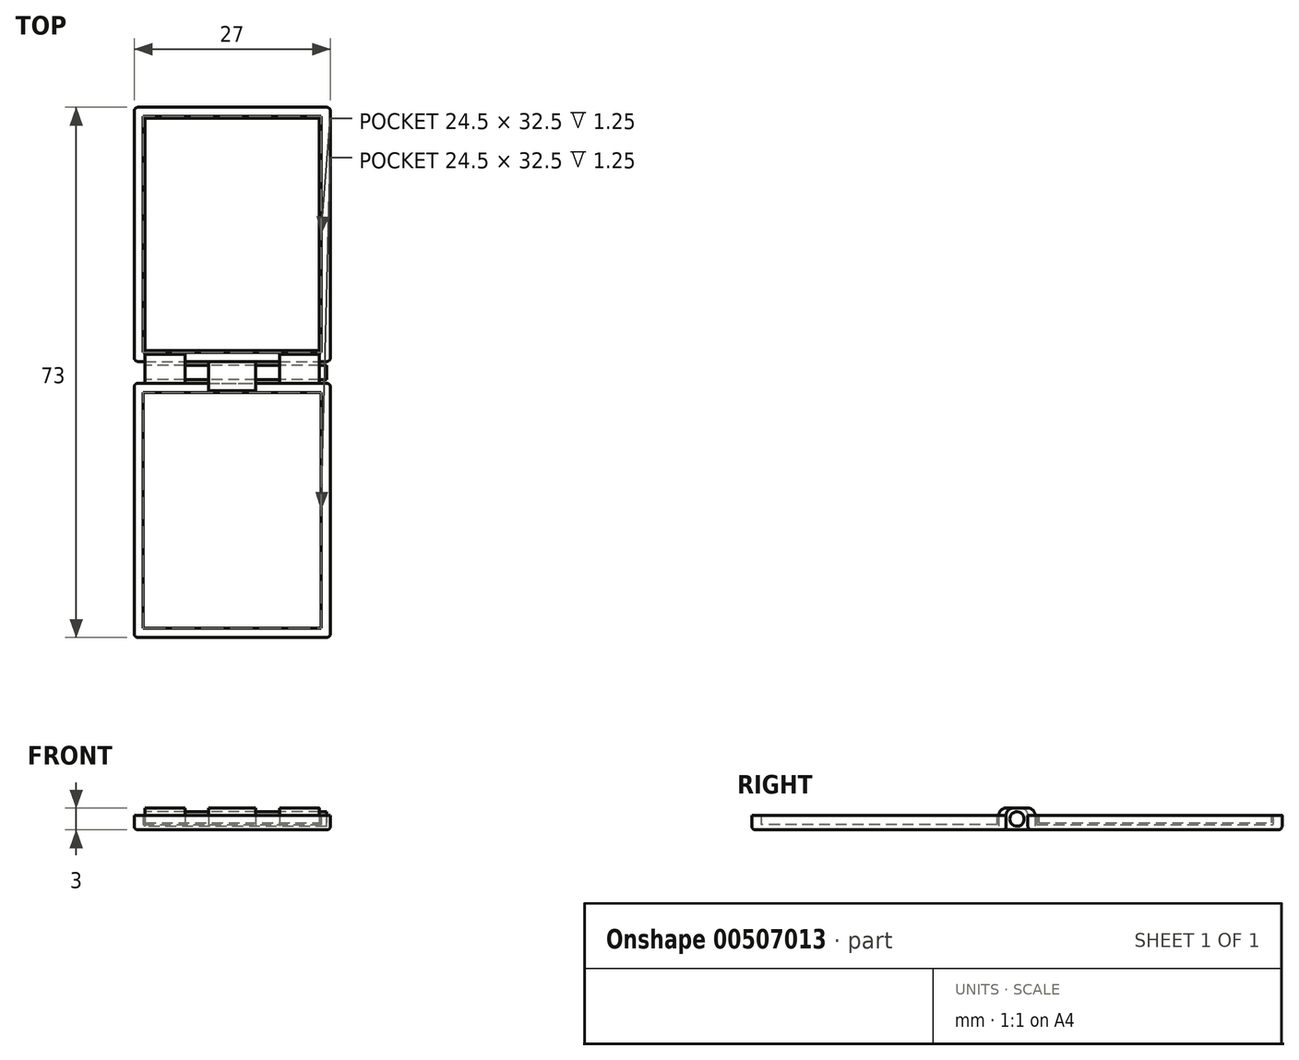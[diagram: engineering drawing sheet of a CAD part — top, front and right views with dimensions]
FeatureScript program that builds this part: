
annotation { "Feature Type Name" : "Feature", "Feature Type Description" : "" }
export const myFeature = defineFeature(function(context is Context, id is Id, definition is map)
    precondition{}
    {
        {
            var Q0;
            Q0=qCreatedBy(makeId("Top.planeOp"),FACE);
            var sketch = newSketch(context, id + "F0", { "sketchPlane" : qUnion([Q0])});
            skLineSegment(sketch, "E0.bottom", {"start": v(0, 0) * mm, "end": v(24, 0) * mm});
            skLineSegment(sketch, "E0.top", {"start": v(0, 32) * mm, "end": v(24, 32) * mm});
            skLineSegment(sketch, "E0.left", {"start": v(0, 0) * mm, "end": v(0, 32) * mm});
            skLineSegment(sketch, "E0.right", {"start": v(24, 0) * mm, "end": v(24, 32) * mm});
            skSolve(sketch);
        }
        {
            var Q0;
            Q0=makeQuery(id+"F0.imprint","IMPRINT",FACE,{"disambiguationData":[TD([[makeQuery(id+"F0.imprint","IMPRINT",EDGE,{"derivedFrom":sQuery(id+"F0.wireOp",EDGE,"E0.bottom")}),1.0]])]});
            extrude(context, id + "F1", {"entities" : qUnion([Q0]), "depth" : 2.1 * mm});
        }
        {
            var Q0;
            Q0=qCreatedBy(makeId("Top.planeOp"),FACE);
            cPlane(context, id + "F2", {"entities" : qUnion([Q0]), "cplaneType" : CPlaneType.OFFSET, "offset" : 1 * mm, "oppositeDirection" : true, "width" : 150 * mm, "height" : 150 * mm});
        }
        {
            var Q0;
            Q0=qCreatedBy(id+"F2.planeOp",FACE);
            var sketch = newSketch(context, id + "F3", { "sketchPlane" : qUnion([Q0])});
            skLineSegment(sketch, "E1.0.0", {"start": v(24, 32) * mm, "end": v(0, 32) * mm});
            skLineSegment(sketch, "E1.0.1", {"start": v(0, 32) * mm, "end": v(0, 0) * mm});
            skLineSegment(sketch, "E1.0.2", {"start": v(0, 0) * mm, "end": v(24, 0) * mm});
            skLineSegment(sketch, "E1.0.3", {"start": v(24, 0) * mm, "end": v(24, 32) * mm});
            skLineSegment(sketch, "E2.0", {"start": v(25.5, 33.5) * mm, "end": v(-1.5, 33.5) * mm});
            skLineSegment(sketch, "E2.1", {"start": v(25.5, -1.5) * mm, "end": v(25.5, 33.5) * mm});
            skLineSegment(sketch, "E2.2", {"start": v(-1.5, -1.5) * mm, "end": v(25.5, -1.5) * mm});
            skLineSegment(sketch, "E2.3", {"start": v(-1.5, 33.5) * mm, "end": v(-1.5, -1.5) * mm});
            skSolve(sketch);
        }
        {
            var Q0;
            Q0=makeQuery(id+"F3.imprint","IMPRINT",FACE,{"disambiguationData":[TD([[makeQuery(id+"F3.imprint","IMPRINT",EDGE,{"derivedFrom":sQuery(id+"F3.wireOp",EDGE,"E1.0.0")}),1.0]])]});
            var Q1;
            Q1=makeQuery(id+"F3.imprint","IMPRINT",FACE,{"disambiguationData":[TD([[makeQuery(id+"F3.imprint","IMPRINT",EDGE,{"derivedFrom":sQuery(id+"F3.wireOp",EDGE,"E1.0.0")}),-1.0]])]});
            extrude(context, id + "F4", {"entities" : qUnion([Q0, Q1]), "depth" : 4 * mm});
        }
        {
            var Q0;
            Q0=makeQuery(id+"F4.opExtrude","SWEPT_FACE",FACE,{"disambiguationData":[OSD([sQuery(id+"F3.wireOp",EDGE,"E2.1")])]});
            var sketch = newSketch(context, id + "F5", { "sketchPlane" : qUnion([Q0])});
            skPoint(sketch, "E3", {"position": v(-1.5, 1) * mm});
            skPoint(sketch, "E4", {"position": v(33.5, 1) * mm});
            skLineSegment(sketch, "E5.bottom", {"start": v(-1.5, 1) * mm, "end": v(33.5, 1) * mm});
            skLineSegment(sketch, "E5.top", {"start": v(-1.5, 3) * mm, "end": v(33.5, 3) * mm});
            skLineSegment(sketch, "E5.left", {"start": v(-1.5, 1) * mm, "end": v(-1.5, 3) * mm});
            skLineSegment(sketch, "E5.right", {"start": v(33.5, 1) * mm, "end": v(33.5, 3) * mm});
            skSolve(sketch);
        }
        {
            var Q0;
            Q0=makeQuery(id+"F1.opExtrude","SWEPT_BODY",BODY,{"disambiguationData":[OSD([sQuery(id+"F0.wireOp",EDGE,"E0.bottom"),sQuery(id+"F0.wireOp",EDGE,"E0.top"),sQuery(id+"F0.wireOp",EDGE,"E0.left"),sQuery(id+"F0.wireOp",EDGE,"E0.right")])]});
            var Q1;
            Q1=makeQuery(id+"F4.opExtrude","SWEPT_BODY",BODY,{"disambiguationData":[OSD([sQuery(id+"F3.wireOp",EDGE,"E2.0"),sQuery(id+"F3.wireOp",EDGE,"E2.1"),sQuery(id+"F3.wireOp",EDGE,"E2.2"),sQuery(id+"F3.wireOp",EDGE,"E2.3")])]});
            var Q2;
            Q2=makeQuery(id+"F1.opExtrude","SWEPT_FACE",FACE,{"disambiguationData":[OSD([sQuery(id+"F0.wireOp",EDGE,"E0.right")])]});
            var Q3;
            Q3=makeQuery(id+"F1.opExtrude","SWEPT_FACE",FACE,{"disambiguationData":[OSD([sQuery(id+"F0.wireOp",EDGE,"E0.left")])]});
            booleanBodies(context, id + "F6", {"operationType" : BooleanOperationType.SUBTRACTION, "tools" : qUnion([Q0]), "targets" : qUnion([Q1]), "offset" : true, "offsetAll" : true, "entitiesToOffset" : qUnion([Q2, Q3]), "offsetDistance" : 0.25 * mm, "keepTools" : true});
        }
        {
            var Q0;
            Q0=makeQuery(id+"F4.opExtrude","SWEPT_EDGE",EDGE,{"disambiguationData":[OSD([sQuery(id+"F3.wireOp",EDGE,"E2.2"),sQuery(id+"F3.wireOp",EDGE,"E2.3")])]});
            var Q1;
            Q1=makeQuery(id+"F4.opExtrude","SWEPT_EDGE",EDGE,{"disambiguationData":[OSD([sQuery(id+"F3.wireOp",EDGE,"E2.1"),sQuery(id+"F3.wireOp",EDGE,"E2.2")])]});
            var Q2;
            Q2=makeQuery(id+"F4.opExtrude","SWEPT_EDGE",EDGE,{"disambiguationData":[OSD([sQuery(id+"F3.wireOp",EDGE,"E2.0"),sQuery(id+"F3.wireOp",EDGE,"E2.1")])]});
            var Q3;
            Q3=makeQuery(id+"F4.opExtrude","SWEPT_EDGE",EDGE,{"disambiguationData":[OSD([sQuery(id+"F3.wireOp",EDGE,"E2.0"),sQuery(id+"F3.wireOp",EDGE,"E2.3")])]});
            var Q4;
            Q4=makeQuery(id+"F4.opExtrude","CAP_EDGE",EDGE,{"disambiguationData":[OSD([sQuery(id+"F3.wireOp",EDGE,"E2.3")])],"isStart":false});
            var Q5;
            Q5=makeQuery(id+"F4.opExtrude","CAP_EDGE",EDGE,{"disambiguationData":[OSD([sQuery(id+"F3.wireOp",EDGE,"E2.0")])],"isStart":false});
            var Q6;
            Q6=makeQuery(id+"F4.opExtrude","CAP_EDGE",EDGE,{"disambiguationData":[OSD([sQuery(id+"F3.wireOp",EDGE,"E2.0")])],"isStart":true});
            var Q7;
            Q7=makeQuery(id+"F4.opExtrude","CAP_EDGE",EDGE,{"disambiguationData":[OSD([sQuery(id+"F3.wireOp",EDGE,"E2.3")])],"isStart":true});
            var Q8;
            Q8=makeQuery(id+"F4.opExtrude","CAP_EDGE",EDGE,{"disambiguationData":[OSD([sQuery(id+"F3.wireOp",EDGE,"E2.1")])],"isStart":false});
            var Q9;
            Q9=makeQuery(id+"F4.opExtrude","CAP_EDGE",EDGE,{"disambiguationData":[OSD([sQuery(id+"F3.wireOp",EDGE,"E2.1")])],"isStart":true});
            var Q10;
            Q10=makeQuery(id+"F4.opExtrude","CAP_EDGE",EDGE,{"disambiguationData":[OSD([sQuery(id+"F3.wireOp",EDGE,"E2.2")])],"isStart":false});
            var Q11;
            Q11=makeQuery(id+"F4.opExtrude","CAP_EDGE",EDGE,{"disambiguationData":[OSD([sQuery(id+"F3.wireOp",EDGE,"E2.2")])],"isStart":true});
            fillet(context, id + "F7", {"entities" : qUnion([Q0, Q1, Q2, Q3, Q4, Q5, Q6, Q7, Q8, Q9, Q10, Q11]), "radius" : 0.5 * mm, "tangentPropagation" : true, "allowEdgeOverflow" : false});
        }
        {
            var Q0;
            Q0=makeQuery(id+"F5.imprint","IMPRINT",FACE,{"disambiguationData":[TD([[makeQuery(id+"F5.imprint","IMPRINT",EDGE,{"derivedFrom":sQuery(id+"F5.wireOp",EDGE,"E5.bottom")}),1.0]])]});
            var Q1;
            Q1=makeQuery(id+"F4.opExtrude","SWEPT_FACE",FACE,{"disambiguationData":[OSD([sQuery(id+"F3.wireOp",EDGE,"E2.3")])]});
            extrude(context, id + "F8", {"entities" : qUnion([Q0]), "operationType" : NewBodyOperationType.REMOVE, "endBound" : BoundingType.UP_TO_SURFACE, "oppositeDirection" : true, "endBoundEntityFace" : qUnion([Q1]), "depth" : 25 * mm});
        }
        {
            var Q0;
            Q0=qCreatedBy(makeId("Front.planeOp"),FACE);
            cPlane(context, id + "F9", {"entities" : qUnion([Q0]), "cplaneType" : CPlaneType.OFFSET, "offset" : 3 * mm, "width" : 150 * mm, "height" : 150 * mm});
        }
        {
            var Q0;
            Q0=makeQuery(id+"F4.opExtrude","SWEPT_BODY",BODY,{"disambiguationData":[OSD([sQuery(id+"F3.wireOp",EDGE,"E2.0"),sQuery(id+"F3.wireOp",EDGE,"E2.1"),sQuery(id+"F3.wireOp",EDGE,"E2.2"),sQuery(id+"F3.wireOp",EDGE,"E2.3")])]});
            var Q1;
            Q1=qCreatedBy(id+"F9.planeOp",FACE);
            mirror(context, id + "F10", {"entities" : qUnion([Q0]), "mirrorPlane" : qUnion([Q1])});
        }
        {
            var Q0;
            Q0=qCreatedBy(id+"F2.planeOp",FACE);
            var sketch = newSketch(context, id + "F11", { "sketchPlane" : qUnion([Q0])});
            skLineSegment(sketch, "E6.0", {"start": v(-1, -1.5) * mm, "end": v(25, -1.5) * mm, "construction": true});
            skLineSegment(sketch, "E7.0", {"start": v(-1, -4.5) * mm, "end": v(25, -4.5) * mm, "construction": true});
            skLineSegment(sketch, "E8", {"start": v(-1, -1.5) * mm, "end": v(-1, -4.5) * mm, "construction": true});
            skLineSegment(sketch, "E9", {"start": v(25, -4.5) * mm, "end": v(25, -1.5) * mm, "construction": true});
            skPoint(sketch, "E10", {"position": v(12, -1.5) * mm});
            skPoint(sketch, "E11", {"position": v(12, -4.5) * mm});
            skPoint(sketch, "E12", {"position": v(-1, -3) * mm});
            skPoint(sketch, "E13", {"position": v(25, -3) * mm});
            skLineSegment(sketch, "E14", {"start": v(12, -1.5) * mm, "end": v(12, -4.5) * mm, "construction": true});
            skPoint(sketch, "E15", {"position": v(12, -3) * mm});
            skLineSegment(sketch, "E16", {"start": v(-1, -3) * mm, "end": v(12, -3) * mm, "construction": true});
            skLineSegment(sketch, "E17", {"start": v(12, -3) * mm, "end": v(25, -3) * mm, "construction": true});
            skPoint(sketch, "E18", {"position": v(5.5, -3) * mm});
            skPoint(sketch, "E19", {"position": v(18.5, -3) * mm});
            skLineSegment(sketch, "E20", {"start": v(18.5, -3) * mm, "end": v(18.5, -4.5) * mm, "construction": true});
            skLineSegment(sketch, "E21", {"start": v(18.5, -4.5) * mm, "end": v(18.5, -3) * mm, "construction": true});
            skLineSegment(sketch, "E22", {"start": v(18.5, -1.5) * mm, "end": v(18.5, -3) * mm, "construction": true});
            skLineSegment(sketch, "E23", {"start": v(5.5, -3) * mm, "end": v(5.5, -4.5) * mm, "construction": true});
            skLineSegment(sketch, "E24", {"start": v(5.5, -4.5) * mm, "end": v(5.5, -3) * mm, "construction": true});
            skLineSegment(sketch, "E25", {"start": v(5.5, -1.5) * mm, "end": v(5.5, -3) * mm, "construction": true});
            skLineSegment(sketch, "E26.bottom", {"start": v(-1, -1.5) * mm, "end": v(5.5, -1.5) * mm});
            skLineSegment(sketch, "E26.top", {"start": v(-1, -4.5) * mm, "end": v(5.5, -4.5) * mm});
            skLineSegment(sketch, "E26.left", {"start": v(-1, -1.5) * mm, "end": v(-1, -4.5) * mm});
            skLineSegment(sketch, "E26.right", {"start": v(5.5, -1.5) * mm, "end": v(5.5, -4.5) * mm});
            skLineSegment(sketch, "E27.bottom", {"start": v(18.5, -1.5) * mm, "end": v(25, -1.5) * mm});
            skLineSegment(sketch, "E27.top", {"start": v(18.5, -4.5) * mm, "end": v(25, -4.5) * mm});
            skLineSegment(sketch, "E27.left", {"start": v(18.5, -1.5) * mm, "end": v(18.5, -4.5) * mm});
            skLineSegment(sketch, "E27.right", {"start": v(25, -1.5) * mm, "end": v(25, -4.5) * mm});
            skLineSegment(sketch, "E28.bottom", {"start": v(8.75, -1.5) * mm, "end": v(15.25, -1.5) * mm});
            skLineSegment(sketch, "E28.top", {"start": v(8.75, -4.5) * mm, "end": v(15.25, -4.5) * mm});
            skLineSegment(sketch, "E28.left", {"start": v(8.75, -1.5) * mm, "end": v(8.75, -4.5) * mm});
            skLineSegment(sketch, "E28.right", {"start": v(15.25, -1.5) * mm, "end": v(15.25, -4.5) * mm});
            skPoint(sketch, "E29", {"position": v(25, -1.5) * mm});
            skLineSegment(sketch, "E30", {"start": v(18.5, -1.5) * mm, "end": v(18.5, -0.5) * mm});
            skLineSegment(sketch, "E31", {"start": v(5.5, -1.5) * mm, "end": v(5.5, -0.5) * mm});
            skLineSegment(sketch, "E32", {"start": v(8.75, -1.5) * mm, "end": v(8.75, -0.5) * mm});
            skLineSegment(sketch, "E33", {"start": v(15.25, -1.5) * mm, "end": v(15.25, -0.5) * mm});
            skLineSegment(sketch, "E34", {"start": v(0, -5.5) * mm, "end": v(5.5, -5.5) * mm});
            skLineSegment(sketch, "E35", {"start": v(5.5, -4.5) * mm, "end": v(5.5, -5.5) * mm});
            skLineSegment(sketch, "E36", {"start": v(8.75, -4.5) * mm, "end": v(8.75, -5.5) * mm});
            skLineSegment(sketch, "E37", {"start": v(15.25, -4.5) * mm, "end": v(15.25, -5.5) * mm});
            skLineSegment(sketch, "E38", {"start": v(18.5, -4.5) * mm, "end": v(18.5, -5.5) * mm});
            skPoint(sketch, "E39", {"position": v(0, -0.5) * mm});
            skPoint(sketch, "E40", {"position": v(24, -0.5) * mm});
            skPoint(sketch, "E41", {"position": v(24, -5.5) * mm});
            skPoint(sketch, "E42", {"position": v(0, -5.5) * mm});
            skLineSegment(sketch, "E43", {"start": v(24, -5.5) * mm, "end": v(24, -1.5) * mm});
            skPoint(sketch, "E44", {"position": v(0, -1.5) * mm});
            skPoint(sketch, "E45", {"position": v(24, -1.5) * mm});
            skPoint(sketch, "E46", {"position": v(24, -4.5) * mm});
            skPoint(sketch, "E47", {"position": v(0, -4.5) * mm});
            skLineSegment(sketch, "E48", {"start": v(24, -1.5) * mm, "end": v(24, -0.5) * mm});
            skLineSegment(sketch, "E49", {"start": v(18.5, -1.5) * mm, "end": v(24, -1.5) * mm});
            skLineSegment(sketch, "E50", {"start": v(0, -1.5) * mm, "end": v(5.5, -1.5) * mm});
            skPoint(sketch, "E51", {"position": v(-1, -0.5) * mm});
            skPoint(sketch, "E52", {"position": v(25, -0.5) * mm});
            skLineSegment(sketch, "E53", {"start": v(0, -0.5) * mm, "end": v(5.5, -0.5) * mm});
            skLineSegment(sketch, "E54", {"start": v(18.5, -0.5) * mm, "end": v(24, -0.5) * mm});
            skLineSegment(sketch, "E55.trimOffspring", {"start": v(8.75, -5.5) * mm, "end": v(15.25, -5.5) * mm});
            skLineSegment(sketch, "E56.trimOffspring", {"start": v(18.5, -5.5) * mm, "end": v(24, -5.5) * mm});
            skLineSegment(sketch, "E57", {"start": v(8.75, -0.5) * mm, "end": v(15.25, -0.5) * mm});
            skLineSegment(sketch, "E58", {"start": v(0, -1.5) * mm, "end": v(0, -0.5) * mm});
            skLineSegment(sketch, "E59", {"start": v(0, -5.5) * mm, "end": v(0, -4.5) * mm});
            skLineSegment(sketch, "E60", {"start": v(0, -1.5) * mm, "end": v(0, -4.5) * mm});
            skSolve(sketch);
        }
        {
            var Q0;
            Q0=makeQuery(id+"F11.imprint","IMPRINT",FACE,{"disambiguationData":[TD([[makeQuery(id+"F11.imprint","IMPRINT",EDGE,{"derivedFrom":sQuery(id+"F11.wireOp",EDGE,"E28.bottom")}),-1.0]])]});
            var Q1;
            {var subQ0=sQuery(id+"F11.wireOp",EDGE,"E27.left");Q1=makeQuery(id+"F11.imprint","IMPRINT",FACE,{"disambiguationData":[TD([[makeQuery(id+"F11.imprint","IMPRINT",EDGE,{"derivedFrom":subQ0}),1.0]])]});}
            var Q2;
            Q2=makeQuery(id+"F11.imprint","IMPRINT",FACE,{"disambiguationData":[TD([[makeQuery(id+"F11.imprint","IMPRINT",EDGE,{"derivedFrom":sQuery(id+"F11.wireOp",EDGE,"E30")}),-1.0]])]});
            var Q3;
            Q3=makeQuery(id+"F11.imprint","IMPRINT",FACE,{"disambiguationData":[TD([[makeQuery(id+"F11.imprint","IMPRINT",EDGE,{"derivedFrom":sQuery(id+"F11.wireOp",EDGE,"E28.top")}),-1.0]])]});
            var Q4;
            Q4=makeQuery(id+"F11.imprint","IMPRINT",FACE,{"disambiguationData":[TD([[makeQuery(id+"F11.imprint","IMPRINT",EDGE,{"derivedFrom":sQuery(id+"F11.wireOp",EDGE,"E31")}),1.0]])]});
            var Q5;
            {var subQ0=sQuery(id+"F11.wireOp",EDGE,"E26.right");Q5=makeQuery(id+"F11.imprint","IMPRINT",FACE,{"disambiguationData":[TD([[makeQuery(id+"F11.imprint","IMPRINT",EDGE,{"derivedFrom":subQ0}),-1.0]])]});}
            extrude(context, id + "F12", {"entities" : qUnion([Q0, Q1, Q2, Q3, Q4, Q5]), "depth" : 3 * mm});
        }
        {
            var Q0;
            Q0=makeQuery(id+"F12.opExtrude","SWEPT_FACE",FACE,{"disambiguationData":[OSD([sQuery(id+"F11.wireOp",EDGE,"E58"),sQuery(id+"F11.wireOp",EDGE,"E60")])]});
            var sketch = newSketch(context, id + "F13", { "sketchPlane" : qUnion([Q0])});
            skPoint(sketch, "E61", {"position": v(3, 0.5) * mm});
            skCircle(sketch, "E62", {"center": v(3, 0.5) * mm, "radius": 1 * mm});
            skPoint(sketch, "E63", {"position": v(0.5, 0.5) * mm});
            skPoint(sketch, "E64", {"position": v(3, 2) * mm});
            skSolve(sketch);
        }
        {
            var Q0;
            Q0 = qSketchRegion(id + "F13", true);
            extrude(context, id + "F14", {"entities" : qUnion([Q0]), "oppositeDirection" : true, "depth" : 25 * mm});
        }
        {
            var Q0;
            Q0=makeQuery(id+"F12.opExtrude","CAP_EDGE",EDGE,{"disambiguationData":[OSD([sQuery(id+"F11.wireOp",EDGE,"E56.trimOffspring")])],"isStart":false});
            var Q1;
            Q1=makeQuery(id+"F12.opExtrude","CAP_EDGE",EDGE,{"disambiguationData":[OSD([sQuery(id+"F11.wireOp",EDGE,"E55.trimOffspring")])],"isStart":false});
            var Q2;
            Q2=makeQuery(id+"F12.opExtrude","CAP_EDGE",EDGE,{"disambiguationData":[OSD([sQuery(id+"F11.wireOp",EDGE,"E34")])],"isStart":false});
            var Q3;
            Q3=makeQuery(id+"F12.opExtrude","CAP_EDGE",EDGE,{"disambiguationData":[OSD([sQuery(id+"F11.wireOp",EDGE,"E53")])],"isStart":false});
            var Q4;
            Q4=makeQuery(id+"F12.opExtrude","CAP_EDGE",EDGE,{"disambiguationData":[OSD([sQuery(id+"F11.wireOp",EDGE,"E57")])],"isStart":false});
            var Q5;
            Q5=makeQuery(id+"F12.opExtrude","CAP_EDGE",EDGE,{"disambiguationData":[OSD([sQuery(id+"F11.wireOp",EDGE,"E54")])],"isStart":false});
            var Q6;
            Q6=makeQuery(id+"F12.opExtrude","CAP_EDGE",EDGE,{"disambiguationData":[OSD([sQuery(id+"F11.wireOp",EDGE,"E27.top")])],"isStart":false});
            var Q7;
            Q7=makeQuery(id+"F12.opExtrude","CAP_EDGE",EDGE,{"disambiguationData":[OSD([sQuery(id+"F11.wireOp",EDGE,"E26.top")])],"isStart":false});
            var Q8;
            Q8=makeQuery(id+"F12.opExtrude","CAP_EDGE",EDGE,{"disambiguationData":[OSD([sQuery(id+"F11.wireOp",EDGE,"E28.bottom")])],"isStart":false});
            fillet(context, id + "F15", {"entities" : qUnion([Q0, Q1, Q2, Q3, Q4, Q5, Q6, Q7, Q8]), "radius" : 1 * mm, "tangentPropagation" : true, "allowEdgeOverflow" : false});
        }
    });
